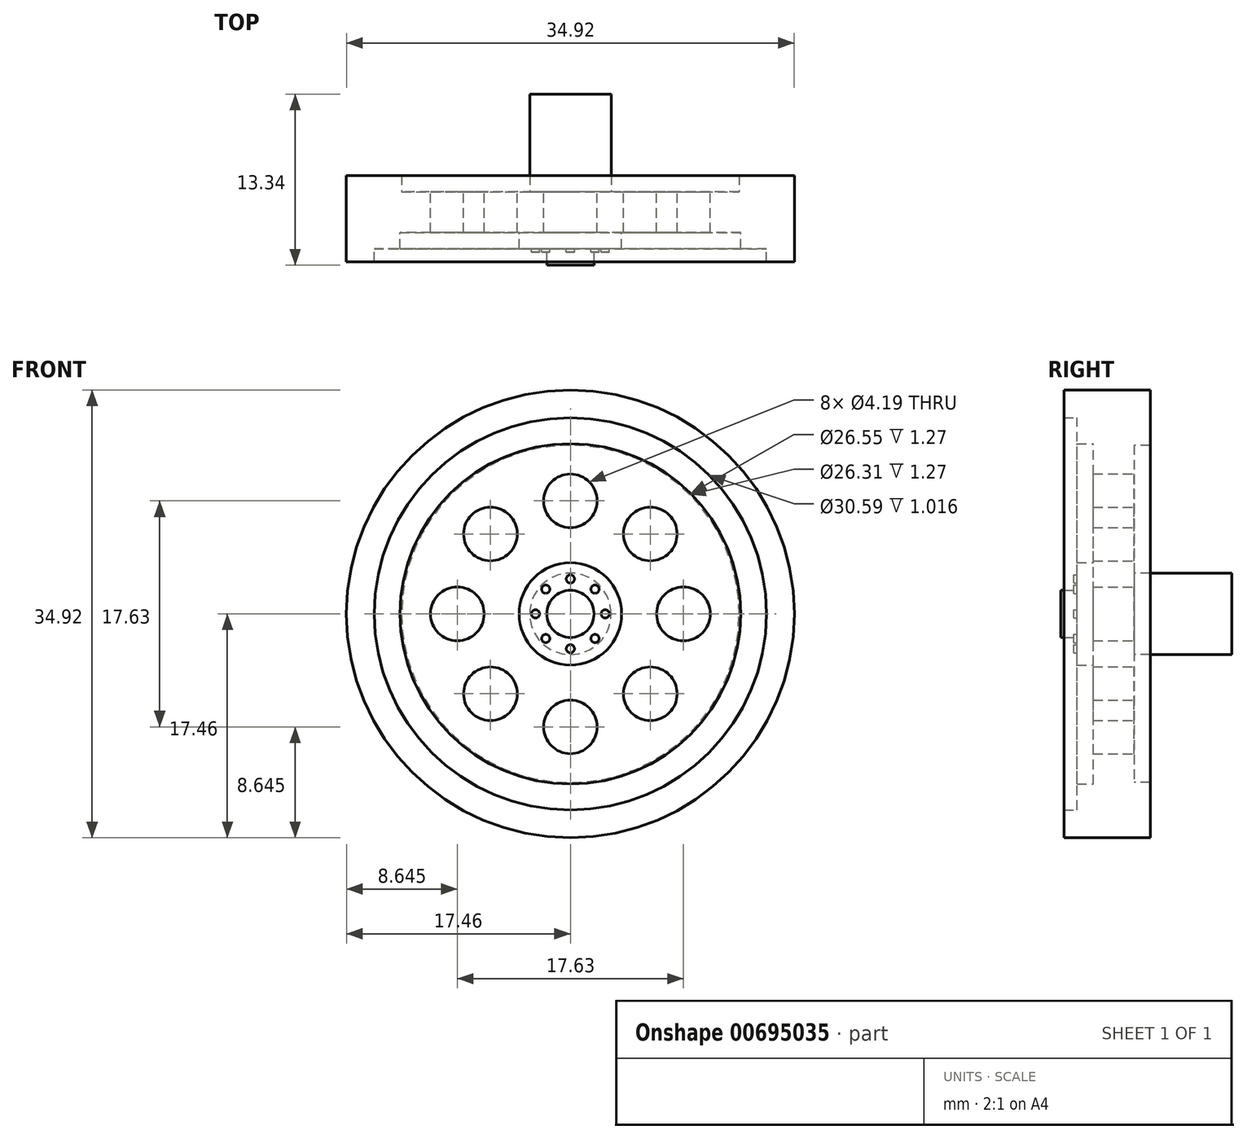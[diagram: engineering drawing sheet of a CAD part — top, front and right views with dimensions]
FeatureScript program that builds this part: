
annotation { "Feature Type Name" : "Feature", "Feature Type Description" : "" }
export const myFeature = defineFeature(function(context is Context, id is Id, definition is map)
    precondition{}
    {
        {
            var Q0;
            Q0=qCreatedBy(makeId("Front.planeOp"),FACE);
            var sketch = newSketch(context, id + "F0", { "sketchPlane" : qUnion([Q0])});
            skCircle(sketch, "E0", {"center": v(0, 0) * mm, "radius": 17.46 * mm});
            skCircle(sketch, "E1", {"center": v(0, 0) * mm, "radius": 12.7 * mm});
            skCircle(sketch, "E2", {"center": v(0, 0) * mm, "radius": 5.59 * mm});
            skCircle(sketch, "E3", {"center": v(0, 0) * mm, "radius": 2.41 * mm});
            skCircle(sketch, "E4", {"center": v(0, 8.81) * mm, "radius": 2.1 * mm});
            skCircle(sketch, "E5.1.0", {"center": v(-6.23, 6.23) * mm, "radius": 2.1 * mm});
            skCircle(sketch, "E5.2.0", {"center": v(-8.81, 0) * mm, "radius": 2.1 * mm});
            skCircle(sketch, "E5.3.0", {"center": v(-6.23, -6.23) * mm, "radius": 2.1 * mm});
            skCircle(sketch, "E5.4.0", {"center": v(0, -8.81) * mm, "radius": 2.1 * mm});
            skCircle(sketch, "E5.5.0", {"center": v(6.23, -6.23) * mm, "radius": 2.1 * mm});
            skCircle(sketch, "E5.6.0", {"center": v(8.81, 0) * mm, "radius": 2.1 * mm});
            skCircle(sketch, "E5.7.0", {"center": v(6.23, 6.23) * mm, "radius": 2.1 * mm});
            skSolve(sketch);
        }
        {
            var Q0;
            Q0=makeQuery(id+"F0.imprint","IMPRINT",FACE,{"disambiguationData":[TD([[makeQuery(id+"F0.imprint","IMPRINT",EDGE,{"derivedFrom":sQuery(id+"F0.wireOp",EDGE,"E0")}),1.0]])]});
            var Q1;
            Q1=makeQuery(id+"F0.imprint","IMPRINT",FACE,{"disambiguationData":[TD([[makeQuery(id+"F0.imprint","IMPRINT",EDGE,{"derivedFrom":sQuery(id+"F0.wireOp",EDGE,"E1")}),1.0]])]});
            var Q2;
            Q2=makeQuery(id+"F0.imprint","IMPRINT",FACE,{"disambiguationData":[TD([[makeQuery(id+"F0.imprint","IMPRINT",EDGE,{"derivedFrom":sQuery(id+"F0.wireOp",EDGE,"E2")}),1.0]])]});
            var Q3;
            Q3=makeQuery(id+"F0.imprint","IMPRINT",FACE,{"disambiguationData":[TD([[makeQuery(id+"F0.imprint","IMPRINT",EDGE,{"derivedFrom":sQuery(id+"F0.wireOp",EDGE,"E3")}),1.0]])]});
            extrude(context, id + "F1", {"entities" : qUnion([Q0, Q1, Q2, Q3]), "depth" : 3.17 * mm, "offsetDistance" : 25.4 * mm});
        }
        {
            var Q0;
            Q0=makeQuery(id+"F1.opExtrude","CAP_FACE",FACE,{"disambiguationData":[OSD([sQuery(id+"F0.wireOp",EDGE,"E0"),sQuery(id+"F0.wireOp",EDGE,"E4"),sQuery(id+"F0.wireOp",EDGE,"E5.1.0"),sQuery(id+"F0.wireOp",EDGE,"E5.2.0"),sQuery(id+"F0.wireOp",EDGE,"E5.3.0"),sQuery(id+"F0.wireOp",EDGE,"E5.4.0"),sQuery(id+"F0.wireOp",EDGE,"E5.5.0"),sQuery(id+"F0.wireOp",EDGE,"E5.6.0"),sQuery(id+"F0.wireOp",EDGE,"E5.7.0")])],"isStart":false});
            var sketch = newSketch(context, id + "F2", { "sketchPlane" : qUnion([Q0])});
            skCircle(sketch, "E6", {"center": v(0, 0) * mm, "radius": 4 * mm});
            skCircle(sketch, "E7", {"center": v(0, 0) * mm, "radius": 1.92 * mm});
            skSolve(sketch);
        }
        {
            var Q0;
            Q0 = qSketchRegion(id + "F2", true);
            var Q1;
            Q1=makeQuery(id+"F2.imprint","IMPRINT",FACE,{"disambiguationData":[TD([[makeQuery(id+"F2.imprint","IMPRINT",EDGE,{"derivedFrom":sQuery(id+"F2.wireOp",EDGE,"E7")}),1.0]])]});
            extrude(context, id + "F3", {"entities" : qUnion([Q0, Q1]), "operationType" : NewBodyOperationType.ADD, "depth" : 1.27 * mm, "offsetDistance" : 25.4 * mm});
        }
        {
            var Q0;
            Q0=makeQuery(id+"F3.opExtrude","CAP_FACE",FACE,{"disambiguationData":[OSD([sQuery(id+"F2.wireOp",EDGE,"E6")])],"isStart":false});
            var sketch = newSketch(context, id + "F4", { "sketchPlane" : qUnion([Q0])});
            skCircle(sketch, "E8", {"center": v(0, 0) * mm, "radius": 1.84 * mm});
            skSolve(sketch);
        }
        {
            var Q0;
            Q0 = qSketchRegion(id + "F4", true);
            extrude(context, id + "F5", {"entities" : qUnion([Q0]), "operationType" : NewBodyOperationType.ADD, "depth" : 1.27 * mm, "offsetDistance" : 25.4 * mm});
        }
        {
            var Q0;
            Q0=makeQuery(id+"F1.opExtrude","CAP_FACE",FACE,{"disambiguationData":[OSD([sQuery(id+"F0.wireOp",EDGE,"E0"),sQuery(id+"F0.wireOp",EDGE,"E4"),sQuery(id+"F0.wireOp",EDGE,"E5.1.0"),sQuery(id+"F0.wireOp",EDGE,"E5.2.0"),sQuery(id+"F0.wireOp",EDGE,"E5.3.0"),sQuery(id+"F0.wireOp",EDGE,"E5.4.0"),sQuery(id+"F0.wireOp",EDGE,"E5.5.0"),sQuery(id+"F0.wireOp",EDGE,"E5.6.0"),sQuery(id+"F0.wireOp",EDGE,"E5.7.0")])],"isStart":true});
            var sketch = newSketch(context, id + "F6", { "sketchPlane" : qUnion([Q0])});
            skCircle(sketch, "E9", {"center": v(0, 0) * mm, "radius": 3.18 * mm});
            skSolve(sketch);
        }
        {
            var Q0;
            Q0=makeQuery(id+"F6.imprint","IMPRINT",FACE,{"disambiguationData":[TD([[makeQuery(id+"F6.imprint","IMPRINT",EDGE,{"derivedFrom":sQuery(id+"F6.wireOp",EDGE,"E9")}),1.0]])]});
            extrude(context, id + "F7", {"entities" : qUnion([Q0]), "operationType" : NewBodyOperationType.ADD, "depth" : 7.62 * mm, "offsetDistance" : 25.4 * mm});
        }
        {
            var Q0;
            Q0=makeQuery(id+"F3.opExtrude","CAP_FACE",FACE,{"disambiguationData":[OSD([sQuery(id+"F2.wireOp",EDGE,"E6")])],"isStart":false});
            var sketch = newSketch(context, id + "F8", { "sketchPlane" : qUnion([Q0])});
            skCircle(sketch, "E10", {"center": v(0, 2.72) * mm, "radius": 0.32 * mm});
            skCircle(sketch, "E11.1.0", {"center": v(-1.92, 1.92) * mm, "radius": 0.32 * mm});
            skCircle(sketch, "E11.2.0", {"center": v(-2.72, 0) * mm, "radius": 0.32 * mm});
            skCircle(sketch, "E11.3.0", {"center": v(-1.92, -1.92) * mm, "radius": 0.32 * mm});
            skCircle(sketch, "E11.4.0", {"center": v(0, -2.72) * mm, "radius": 0.32 * mm});
            skCircle(sketch, "E11.5.0", {"center": v(1.92, -1.92) * mm, "radius": 0.32 * mm});
            skCircle(sketch, "E11.6.0", {"center": v(2.72, 0) * mm, "radius": 0.32 * mm});
            skCircle(sketch, "E11.7.0", {"center": v(1.92, 1.92) * mm, "radius": 0.32 * mm});
            skPoint(sketch, "E11.center", {"position": v(0, 0) * mm});
            skSolve(sketch);
        }
        {
            var Q0;
            Q0 = qSketchRegion(id + "F8", true);
            extrude(context, id + "F9", {"entities" : qUnion([Q0]), "operationType" : NewBodyOperationType.ADD, "depth" : 0.25 * mm, "offsetDistance" : 25.4 * mm});
        }
        {
            var Q0;
            Q0=makeQuery(id+"F1.opExtrude","CAP_FACE",FACE,{"disambiguationData":[OSD([sQuery(id+"F0.wireOp",EDGE,"E0"),sQuery(id+"F0.wireOp",EDGE,"E4"),sQuery(id+"F0.wireOp",EDGE,"E5.1.0"),sQuery(id+"F0.wireOp",EDGE,"E5.2.0"),sQuery(id+"F0.wireOp",EDGE,"E5.3.0"),sQuery(id+"F0.wireOp",EDGE,"E5.4.0"),sQuery(id+"F0.wireOp",EDGE,"E5.5.0"),sQuery(id+"F0.wireOp",EDGE,"E5.6.0"),sQuery(id+"F0.wireOp",EDGE,"E5.7.0")])],"isStart":false});
            var sketch = newSketch(context, id + "F10", { "sketchPlane" : qUnion([Q0])});
            skCircle(sketch, "E12", {"center": v(0, 0) * mm, "radius": 13.28 * mm});
            skSolve(sketch);
        }
        {
            var Q0;
            Q0=makeQuery(id+"F10.imprint","IMPRINT",FACE,{"disambiguationData":[TD([[makeQuery(id+"F10.imprint","IMPRINT",EDGE,{"derivedFrom":sQuery(id+"F10.wireOp",EDGE,"E12")}),-1.0]])]});
            extrude(context, id + "F11", {"entities" : qUnion([Q0]), "operationType" : NewBodyOperationType.ADD, "depth" : 1.27 * mm, "offsetDistance" : 25.4 * mm});
        }
        {
            var Q0;
            Q0=makeQuery(id+"F1.opExtrude","CAP_FACE",FACE,{"disambiguationData":[OSD([sQuery(id+"F0.wireOp",EDGE,"E0"),sQuery(id+"F0.wireOp",EDGE,"E4"),sQuery(id+"F0.wireOp",EDGE,"E5.1.0"),sQuery(id+"F0.wireOp",EDGE,"E5.2.0"),sQuery(id+"F0.wireOp",EDGE,"E5.3.0"),sQuery(id+"F0.wireOp",EDGE,"E5.4.0"),sQuery(id+"F0.wireOp",EDGE,"E5.5.0"),sQuery(id+"F0.wireOp",EDGE,"E5.6.0"),sQuery(id+"F0.wireOp",EDGE,"E5.7.0")])],"isStart":true});
            var sketch = newSketch(context, id + "F12", { "sketchPlane" : qUnion([Q0])});
            skCircle(sketch, "E13", {"center": v(0, 0) * mm, "radius": 13.16 * mm});
            skSolve(sketch);
        }
        {
            var Q0;
            Q0=makeQuery(id+"F12.imprint","IMPRINT",FACE,{"disambiguationData":[TD([[makeQuery(id+"F12.imprint","IMPRINT",EDGE,{"derivedFrom":sQuery(id+"F12.wireOp",EDGE,"E13")}),-1.0]])]});
            extrude(context, id + "F13", {"entities" : qUnion([Q0]), "operationType" : NewBodyOperationType.ADD, "depth" : 1.27 * mm, "offsetDistance" : 25.4 * mm});
        }
        {
            var Q0;
            Q0=makeQuery(id+"F11.opExtrude","CAP_FACE",FACE,{"disambiguationData":[OSD([sQuery(id+"F0.wireOp",EDGE,"E0"),sQuery(id+"F10.wireOp",EDGE,"E12")])],"isStart":false});
            var sketch = newSketch(context, id + "F14", { "sketchPlane" : qUnion([Q0])});
            skCircle(sketch, "E14", {"center": v(0, 0) * mm, "radius": 15.3 * mm});
            skSolve(sketch);
        }
        {
            var Q0;
            Q0=makeQuery(id+"F14.imprint","IMPRINT",FACE,{"disambiguationData":[TD([[makeQuery(id+"F14.imprint","IMPRINT",EDGE,{"derivedFrom":sQuery(id+"F14.wireOp",EDGE,"E14")}),-1.0]])]});
            extrude(context, id + "F15", {"entities" : qUnion([Q0]), "operationType" : NewBodyOperationType.ADD, "depth" : 1.02 * mm, "offsetDistance" : 25.4 * mm});
        }
    });
